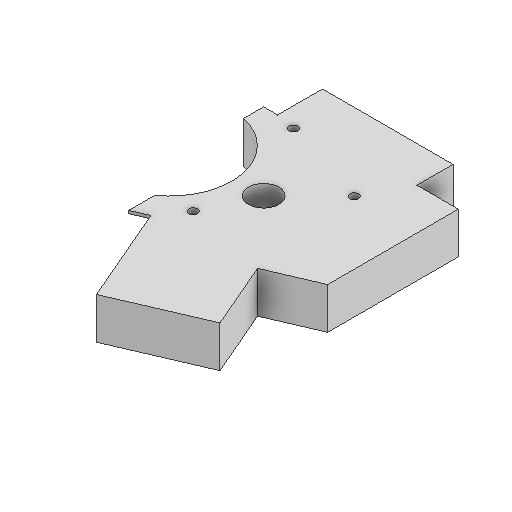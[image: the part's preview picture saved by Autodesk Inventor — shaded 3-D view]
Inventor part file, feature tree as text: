
AUTODESK INVENTOR PART (.ipt)
format: ipt  version: 2022 (Build 260153000, 153)  size: 649,216 bytes
history: native  units: mm
features: extrude x8, sketch x8, projected_geometry x8, other x4, reference x1
ambient origin geometry x8: Origin, YZ Plane, XZ Plane, XY Plane, X Axis, Y Axis, Z Axis, Center Point
bodies: Volumenkörper1 (feature_tree)
feature tree (29):
  extrude  "Extrusion1"  Depth=9.5mm
  extrude  "Extrusion2"  Depth=30.0mm
  extrude  "Extrusion3"  Depth=3.2mm
  extrude  "Extrusion4"  Depth=5.1mm
  extrude  "Extrusion5"  TaperAngle=90.0deg  [1 undecoded]
  extrude  "Extrusion6"  Depth=16.5mm
  extrude  "Extrusion7"  TaperAngle=90.0deg  [1 undecoded]
  extrude  "Extrusion8"  Depth=6.0mm
  sketch  "Skizze1"  dims[d0=30.0mm d1=9.5mm]
  other  "Bild1"
  sketch  "Skizze2"  dims[d2=8.3mm d3=30.0mm]
  projected_geometry  "Projizierte Kontur1"
  sketch  "Skizze3"  dims[d4=10.3mm d5=3.2mm]
  projected_geometry  "Projizierte Kontur2"
  sketch  "Skizze4"  dims[d6=4.6mm d7=5.1mm]
  projected_geometry  "Projizierte Kontur3"
  sketch  "Skizze5"  dims[d8=25.5mm d10=90.0deg]
  projected_geometry  "Projizierte Kontur4"
  sketch  "Skizze6"  dims[d11=20.0mm d12=16.5mm]
  reference  "Referenz1"
  sketch  "Skizze7"  dims[d13=21.6mm d14=90.0deg]
  projected_geometry  "Projizierte Kontur5"
  projected_geometry  "Projizierte Kontur6"
  projected_geometry  "Projizierte Kontur7"
  sketch  "Skizze8"  dims[d30=90.0deg d34=6.0mm d36=9.5mm d37=0.0mm d38=14.3mm d39=3.0mm d40=9.5mm d41=0.0mm d42=3.0mm d43=6.0mm d44=9.5mm d45=0.0mm d46=25.0mm d47=28.0mm d48=10.0mm d49=0.0mm d50=3.74mm d51=3.7mm d52=10.0mm d53=0.0mm d54=0.0mm d55=0.0mm d56=7.7mm d57=10.0mm d58=0.0mm d59=2.0mm d60=10.0mm d61=10.0mm d62=0.0mm]
  projected_geometry  "Projizierte Kontur8"
  other  "00_KES_400_BlurayOPU.iam"
  other  "00_KES400:1"
  other  "00_KES400_Bluray_Lens:1"
note: 2 required parameter values undecoded (feature->parameter linkage not recoverable at this tier; creation-order binding heuristic only, values carry confidence <= 0.55)
